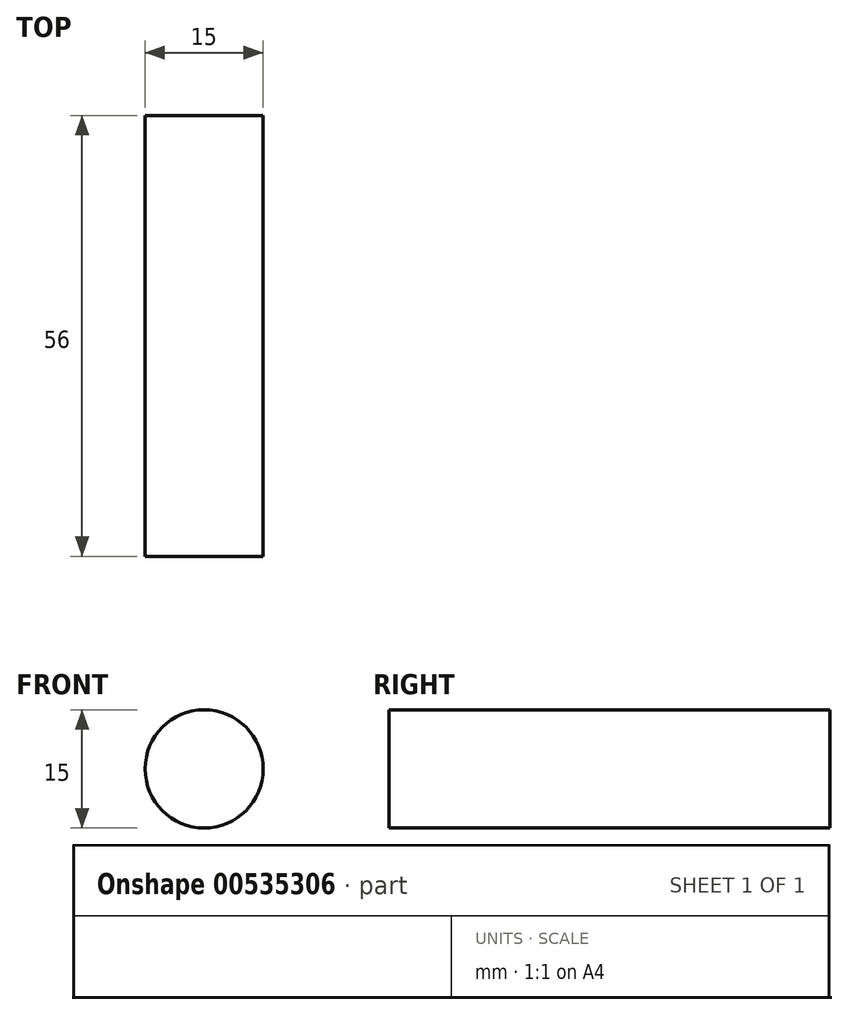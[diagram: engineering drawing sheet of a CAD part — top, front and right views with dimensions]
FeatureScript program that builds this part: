
annotation { "Feature Type Name" : "Feature", "Feature Type Description" : "" }
export const myFeature = defineFeature(function(context is Context, id is Id, definition is map)
    precondition{}
    {
        {
            var Q0;
            Q0=qCreatedBy(makeId("Front.planeOp"),FACE);
            var sketch = newSketch(context, id + "F0", { "sketchPlane" : qUnion([Q0])});
            skCircle(sketch, "E0", {"center": v(0, 0) * mm, "radius": 7.5 * mm});
            skSolve(sketch);
        }
        {
            var Q0;
            Q0 = qSketchRegion(id + "F0", true);
            extrude(context, id + "F1", {"entities" : qUnion([Q0]), "depth" : 56 * mm, "offsetDistance" : 25 * mm});
        }
    });
